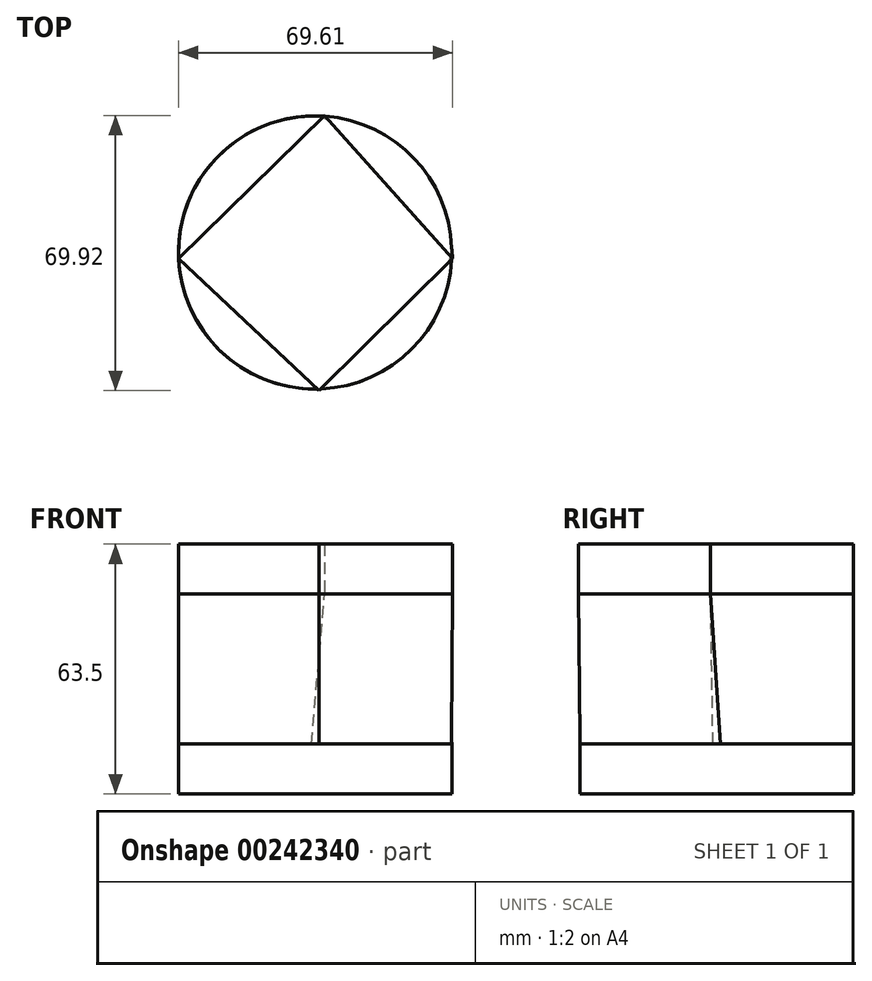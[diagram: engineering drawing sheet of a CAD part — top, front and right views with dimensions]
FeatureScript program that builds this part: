
annotation { "Feature Type Name" : "Feature", "Feature Type Description" : "" }
export const myFeature = defineFeature(function(context is Context, id is Id, definition is map)
    precondition{}
    {
        {
            var Q0;
            Q0=qCreatedBy(makeId("Top.planeOp"),FACE);
            cPlane(context, id + "F0", {"entities" : qUnion([Q0]), "cplaneType" : CPlaneType.OFFSET, "offset" : 50.8 * mm, "width" : 152.4 * mm, "height" : 152.4 * mm});
        }
        {
            var Q0;
            Q0=qCreatedBy(makeId("Top.planeOp"),FACE);
            var sketch = newSketch(context, id + "F1", { "sketchPlane" : qUnion([Q0])});
            skCircle(sketch, "E0", {"center": v(19.97, -18.67) * mm, "radius": 34.7 * mm});
            skSolve(sketch);
        }
        {
            var Q0;
            Q0=makeQuery(id+"F1.imprint","IMPRINT",FACE,{"disambiguationData":[TD([[makeQuery(id+"F1.imprint","IMPRINT",EDGE,{"derivedFrom":sQuery(id+"F1.wireOp",EDGE,"E0")}),1.0]])]});
            extrude(context, id + "F2", {"entities" : qUnion([Q0]), "depth" : 12.7 * mm});
        }
        {
            var Q0;
            Q0=qCreatedBy(id+"F0.planeOp",FACE);
            var sketch = newSketch(context, id + "F3", { "sketchPlane" : qUnion([Q0])});
            skLineSegment(sketch, "E1", {"start": v(20.92, -53.77) * mm, "end": v(54.87, -20.19) * mm});
            skLineSegment(sketch, "E2", {"start": v(54.87, -20.19) * mm, "end": v(22.39, 16.15) * mm});
            skLineSegment(sketch, "E3", {"start": v(22.39, 16.15) * mm, "end": v(-14.68, -20.19) * mm});
            skLineSegment(sketch, "E4", {"start": v(-14.68, -20.19) * mm, "end": v(20.92, -53.77) * mm});
            skSolve(sketch);
        }
        {
            var Q0;
            Q0=makeQuery(id+"F3.imprint","IMPRINT",FACE,{"disambiguationData":[TD([[makeQuery(id+"F3.imprint","IMPRINT",EDGE,{"derivedFrom":sQuery(id+"F3.wireOp",EDGE,"E1")}),1.0]])]});
            extrude(context, id + "F4", {"entities" : qUnion([Q0]), "depth" : 12.7 * mm});
        }
        {
            var Q0;
            Q0=makeQuery(id+"F2.opExtrude","CAP_FACE",FACE,{"disambiguationData":[OSD([sQuery(id+"F1.wireOp",EDGE,"E0")])],"isStart":false});
            var Q1;
            Q1=makeQuery(id+"F4.opExtrude","CAP_FACE",FACE,{"disambiguationData":[OSD([sQuery(id+"F3.wireOp",EDGE,"E1"),sQuery(id+"F3.wireOp",EDGE,"E2"),sQuery(id+"F3.wireOp",EDGE,"E3"),sQuery(id+"F3.wireOp",EDGE,"E4")])],"isStart":true});
            loft(context, id + "F5", {"sheetProfilesArray" : [{ "sheetProfileEntities" : qUnion([Q0]) }, { "sheetProfileEntities" : qUnion([Q1]) }]});
        }
    });
